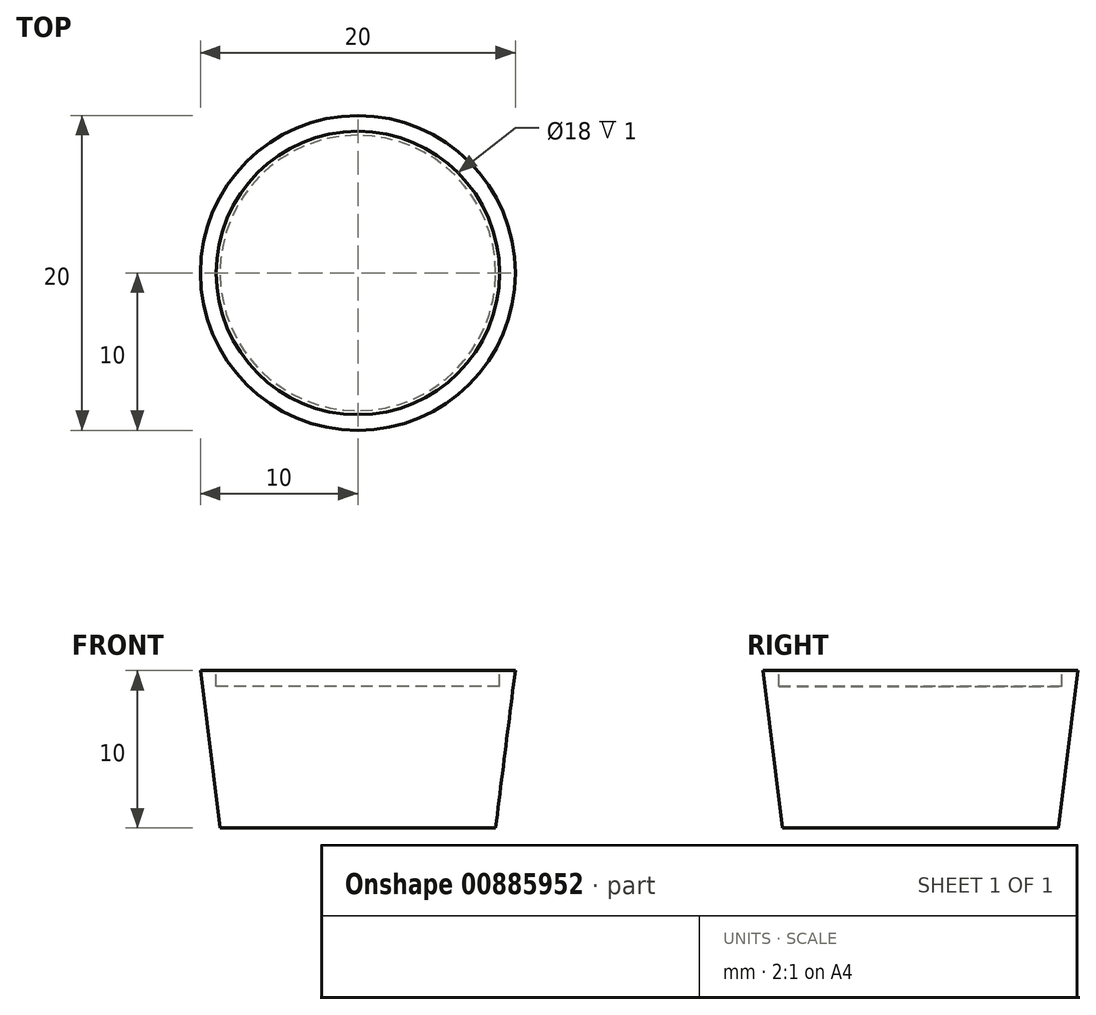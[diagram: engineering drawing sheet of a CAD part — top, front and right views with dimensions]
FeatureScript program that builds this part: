
annotation { "Feature Type Name" : "Feature", "Feature Type Description" : "" }
export const myFeature = defineFeature(function(context is Context, id is Id, definition is map)
    precondition{}
    {
        {
            var Q0;
            Q0=qCreatedBy(makeId("Top.planeOp"),FACE);
            var sketch = newSketch(context, id + "F0", { "sketchPlane" : qUnion([Q0])});
            skCircle(sketch, "E0", {"center": v(0, 0) * mm, "radius": 8.75 * mm});
            skSolve(sketch);
        }
        {
            var Q0;
            Q0=makeQuery(id+"F0.imprint","IMPRINT",FACE,{"disambiguationData":[TD([[makeQuery(id+"F0.imprint","IMPRINT",EDGE,{"derivedFrom":sQuery(id+"F0.wireOp",EDGE,"E0")}),1.0]])]});
            cPlane(context, id + "F1", {"entities" : qUnion([Q0]), "cplaneType" : CPlaneType.OFFSET, "offset" : 10 * mm, "width" : 150 * mm, "height" : 150 * mm});
        }
        {
            var Q0;
            Q0=qCreatedBy(id+"F1.planeOp",FACE);
            var sketch = newSketch(context, id + "F2", { "sketchPlane" : qUnion([Q0])});
            skCircle(sketch, "E1", {"center": v(0, 0) * mm, "radius": 10 * mm});
            skSolve(sketch);
        }
        {
            var Q0;
            Q0=makeQuery(id+"F2.imprint","IMPRINT",FACE,{"disambiguationData":[TD([[makeQuery(id+"F2.imprint","IMPRINT",EDGE,{"derivedFrom":sQuery(id+"F2.wireOp",EDGE,"E1")}),1.0]])]});
            var Q1;
            Q1=makeQuery(id+"F0.imprint","IMPRINT",FACE,{"disambiguationData":[TD([[makeQuery(id+"F0.imprint","IMPRINT",EDGE,{"derivedFrom":sQuery(id+"F0.wireOp",EDGE,"E0")}),1.0]])]});
            loft(context, id + "F3", {"sheetProfilesArray" : [{ "sheetProfileEntities" : qUnion([Q0]) }, { "sheetProfileEntities" : qUnion([Q1]) }]});
        }
        {
            var Q0;
            Q0=makeQuery(id+"F3.opLoft","CAP_FACE",FACE,{"disambiguationData":[OSD([makeQuery(id+"F2.imprint","IMPRINT",FACE,{"disambiguationData":[TD([[makeQuery(id+"F2.imprint","IMPRINT",EDGE,{"derivedFrom":sQuery(id+"F2.wireOp",EDGE,"E1")}),1.0]])]})])],"isStart":true});
            var sketch = newSketch(context, id + "F4", { "sketchPlane" : qUnion([Q0])});
            skCircle(sketch, "E2", {"center": v(0, 0) * mm, "radius": 9 * mm});
            skSolve(sketch);
        }
        {
            var Q0;
            Q0=makeQuery(id+"F4.imprint","IMPRINT",FACE,{"disambiguationData":[TD([[makeQuery(id+"F4.imprint","IMPRINT",EDGE,{"derivedFrom":sQuery(id+"F4.wireOp",EDGE,"E2")}),1.0]])]});
            extrude(context, id + "F5", {"entities" : qUnion([Q0]), "operationType" : NewBodyOperationType.REMOVE, "oppositeDirection" : true, "depth" : 1 * mm, "offsetDistance" : 25 * mm});
        }
    });
